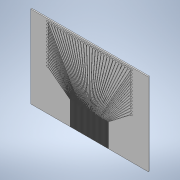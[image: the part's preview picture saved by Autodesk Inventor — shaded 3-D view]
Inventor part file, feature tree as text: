
AUTODESK INVENTOR PART (.ipt)
format: ipt  version: 2021 (Build 250183000, 183)  size: 1,150,976 bytes
history: native  units: in
note: dims shown in document units (in); Inventor stores cm internally (conversion verified against a paired STEP export)
features: extrude x5, sketch x4, projected_geometry x4, pattern_linear x2, mirror x1
ambient origin geometry x8: Origin, YZ Plane, XZ Plane, XY Plane, X Axis, Y Axis, Z Axis, Center Point
bodies: Solid1 (feature_tree)
feature tree (16):
  extrude  "Extrusion1"  Depth=2.7559in
  extrude  "Extrusion2"  Depth=0.0118in
  pattern_linear  "Rectangular Pattern1"  Count1=2  [1 undecoded]
  extrude  "Extrusion3"  Depth=0.0236in
  pattern_linear  "Rectangular Pattern2"  Count1=4  [1 undecoded]
  extrude  "Extrusion4"  Depth=0.0014in
  extrude  "Extrusion5"  Depth=0.0014in TaperAngle=0.0deg
  mirror  "Mirror1"
  sketch  "Sketch1"  dims[d0=3.937in d1=2.7559in]
  sketch  "Sketch2"  dims[d2=0.0394in d3=0.0in d4=0.0118in d5=0.7874in]
  projected_geometry  "Projected Loop1"
  projected_geometry  "Projected Loop2"
  sketch  "Sketch4"  dims[d6=0.0014in d7=0.0in d8=21.6535in d10=0.0236in d11=1.5748in]
  projected_geometry  "Projected Loop3"
  sketch  "Sketch5"  dims[d12=0.1969in d13=0.0689in d16=0.0014in d17=0.0in d18=0.0787in d19=11.4173in d21=0.1in d22=5.5118in d24=0.1in d25=0.0118in d26=0.0118in d27=0.0118in d28=0.0118in d29=0.0118in d30=0.0118in d31=0.0118in d32=0.0118in d33=0.0118in d34=0.0118in d35=0.0118in d36=0.0118in d37=0.0118in d38=0.0118in d39=0.0118in d40=0.0118in d41=0.0118in d42=0.0118in d43=0.0118in d44=0.0118in d45=0.0118in d46=0.0118in d47=0.0118in d48=0.0118in d49=0.0118in d50=0.0118in d51=0.0118in d52=0.0118in d53=0.0014in d54=0.0in d55=0.0295in d56=0.0in d57=0.0in]
  projected_geometry  "Projected Loop4"
note: 2 required parameter values undecoded (feature->parameter linkage not recoverable at this tier; creation-order binding heuristic only, values carry confidence <= 0.55)
